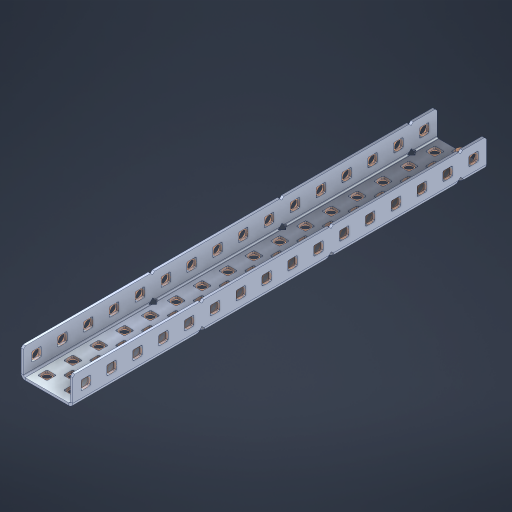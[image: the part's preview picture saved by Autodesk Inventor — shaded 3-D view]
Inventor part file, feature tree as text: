
AUTODESK INVENTOR PART (.ipt)
format: ipt  version: 2023 (Build 270158000, 158)  size: 1,214,976 bytes
history: native  units: in
note: dims shown in document units (in); Inventor stores cm internally (conversion verified against a paired STEP export)
features: other x87, extrude x78, sheet_metal_op x11, sketch x10, pattern_linear x2, mirror x1, chamfer x1
ambient origin geometry x8: Origin, YZ Plane, XZ Plane, XY Plane, X Axis, Y Axis, Z Axis, Center Point
bodies: Solid1 (feature_tree), Body (feature_tree)
feature tree (190):
  sheet_metal_op  "Flanges"
  other  "Flange Pattern Plane"
  other  "Flange Pattern Sketch"
  sheet_metal_op  "Flange Pattern"
  sheet_metal_op  "Body Pattern"
  pattern_linear  "Center Pattern"  Spacing1=0.0469in  [1 undecoded]
  other  "Arc Length"
  mirror  "Notch Mirror"
  pattern_linear  "Notch Pattern"  Spacing1=0.182in  [1 undecoded]
  chamfer  "End Chamfer"
  extrude  "Half Cut"  Depth=0.02in
  sketch  "Sketch1"  dims[d0=1.0in]
  other  "Plate1"
  sketch  "Sketch2"  dims[d1=8.0in]
  other  "Plate2"
  sheet_metal_op  "Bend1"
  sheet_metal_op  "Corner1"
  sketch  "Sketch3"  dims[d2=0.0469in]
  sketch  "Sketch7"  dims[d3=0.0469in]
  other  "Srf1"
  other  "Srf2"
  sketch  "Sketch8"  dims[d4=0.0234in]
  sketch  "Sketch9"  dims[d5=0.0938in]
  other  "Srf91"
  sheet_metal_op  "Body Pattern Sketch"
  other  "Srf92"
  sketch  "Sketch13"  dims[d6=0.0469in]
  sketch  "Sketch14"  dims[d7=0.5in d8=90.0deg d9=0.0312in]
  sketch  "Sketch15"  dims[d10=0.1875in]
  sketch  "Sketch16"  dims[d11=0.0469in d12=0.0469in d16=0.182in d17=0.02in d18=0.0469in d19=0.0in d20=0.25in d21=0.25in d38=6.2992in d40=0.5in d41=0.7874in d43=1.0in d46=0.172in d47=1.0in d48=0.0in d49=0.182in d50=0.02in d51=0.25in d52=0.25in d53=0.0469in d54=0.0in d55=0.172in d56=1.0in d57=0.0in d58=0.25in d60=6.2992in d62=0.5in d63=0.7874in d65=0.5in d85=0.1227in d86=0.1659in d88=0.04in d89=0.0469in d90=0.0in d91=0.04in d92=0.0491in d95=2.5in d96=0.04in d97=0.25in d98=45.0deg d99=0.25in d100=0.5in d101=0.0in d102=2.497in d106=0.182in d107=0.02in d108=0.5in d109=0.5in d110=0.0469in d111=0.0in d112=0.172in d113=0.5in d114=0.0in d117=0.5in d118=0.5in d119=0.5in]
  other  "Srf786"
  other  "Srf823"
  other  "Srf824"
  other  "Srf825"
  other  "Srf826"
  other  "Srf827"
  other  "Srf828"
  other  "Srf829"
  other  "Srf856"
  other  "Srf857"
  other  "Srf858"
  other  "Srf859"
  other  "Srf860"
  other  "Srf861"
  other  "Srf862"
  other  "Srf889"
  other  "Srf890"
  other  "Srf891"
  other  "Srf892"
  other  "Srf893"
  other  "Srf894"
  other  "Srf895"
  other  "Srf896"
  other  "Srf922"
  other  "Srf923"
  other  "Srf924"
  other  "Srf925"
  other  "Srf926"
  other  "Srf959"
  other  "Srf960"
  other  "Srf961"
  other  "Srf962"
  other  "Srf963"
  other  "Srf996"
  other  "Srf997"
  other  "Srf998"
  other  "Srf999"
  other  "Srf1000"
  other  "Srf1143"
  other  "Srf1144"
  other  "Srf1145"
  other  "Srf1146"
  other  "Srf1147"
  other  "Srf1148"
  other  "Srf1149"
  other  "Srf1150"
  other  "Srf1151"
  other  "Srf1152"
  other  "Srf1153"
  other  "Srf1154"
  other  "Srf1155"
  other  "Srf1156"
  other  "Srf1157"
  other  "Srf1158"
  other  "Srf1159"
  other  "Srf1160"
  other  "Srf1199"
  other  "Srf1200"
  other  "Srf1201"
  other  "Srf1202"
  other  "Srf1203"
  other  "Srf1204"
  other  "Srf1205"
  other  "Srf1206"
  other  "Srf1207"
  other  "Srf1208"
  other  "Srf1209"
  other  "Srf1210"
  other  "Srf1211"
  other  "Srf1212"
  other  "Srf1213"
  other  "Srf1214"
  other  "Srf1215"
  other  "Srf1216"
  other  "Srf1255"
  other  "Srf1256"
  sheet_metal_op  "Flange Stamp"
  sheet_metal_op  "Flange Circle"
  sheet_metal_op  "Body Stamp"
  sheet_metal_op  "Body Circle"
  other  "Center Stamp"
  other  "Center Circle"
  sheet_metal_op  "Notch"
  extrude  "ExtrusionSrf2"  Depth=0.0469in
  extrude  "ExtrusionSrf92"  TaperAngle=0.0deg  [1 undecoded]
  extrude  "ExtrusionSrf823"  Depth=0.5in
  extrude  "ExtrusionSrf824"  Depth=0.5in
  extrude  "ExtrusionSrf825"  Depth=0.5in
  extrude  "ExtrusionSrf826"  Depth=0.5in
  extrude  "ExtrusionSrf827"  Depth=1.0in TaperAngle=0.0deg
  extrude  "ExtrusionSrf828"  Depth=0.5in
  extrude  "ExtrusionSrf829"  Depth=0.02in
  extrude  "ExtrusionSrf856"  Depth=0.5in
  extrude  "ExtrusionSrf857"  Depth=0.5in
  extrude  "ExtrusionSrf858"  Depth=0.0469in
  extrude  "ExtrusionSrf859"  TaperAngle=0.0deg  [1 undecoded]
  extrude  "ExtrusionSrf860"  Depth=0.5in
  extrude  "ExtrusionSrf861"  Depth=1.0in TaperAngle=0.0deg
  extrude  "ExtrusionSrf862"  Depth=0.5in
  extrude  "ExtrusionSrf889"  Depth=0.5in
  extrude  "ExtrusionSrf890"  Depth=0.5in
  extrude  "ExtrusionSrf891"  Depth=0.5in
  extrude  "ExtrusionSrf892"  Depth=0.5in
  extrude  "ExtrusionSrf893"  Depth=0.5in
  extrude  "ExtrusionSrf894"  Depth=0.0469in
  extrude  "ExtrusionSrf895"  TaperAngle=0.0deg  [1 undecoded]
  extrude  "ExtrusionSrf896"  Depth=0.5in
  extrude  "ExtrusionSrf922"  Depth=0.5in
  extrude  "ExtrusionSrf923"  Depth=2.5in
  extrude  "ExtrusionSrf924"  Depth=0.5in TaperAngle=45.0deg
  extrude  "ExtrusionSrf925"  Depth=0.5in
  extrude  "ExtrusionSrf926"  Depth=0.5in TaperAngle=0.0deg
  extrude  "ExtrusionSrf959"  Depth=0.5in
  extrude  "ExtrusionSrf960"  Depth=0.5in
  extrude  "ExtrusionSrf961"  Depth=0.02in
  extrude  "ExtrusionSrf962"  Depth=0.5in
  extrude  "ExtrusionSrf963"  Depth=0.5in
  extrude  "ExtrusionSrf996"  Depth=0.0469in
  extrude  "ExtrusionSrf997"  TaperAngle=0.0deg  [1 undecoded]
  extrude  "ExtrusionSrf998"  Depth=0.5in
  extrude  "ExtrusionSrf999"  Depth=0.5in TaperAngle=0.0deg
  extrude  "ExtrusionSrf1000"  Depth=0.5in
  extrude  "ExtrusionSrf1143"  Depth=0.5in
  extrude  "ExtrusionSrf1144"  Depth=0.5in
  extrude  "ExtrusionSrf1145"  [1 undecoded]
  extrude  "ExtrusionSrf1146"  [1 undecoded]
  extrude  "ExtrusionSrf1147"  [1 undecoded]
  extrude  "ExtrusionSrf1148"  [1 undecoded]
  extrude  "ExtrusionSrf1149"  [1 undecoded]
  extrude  "ExtrusionSrf1150"  [1 undecoded]
  extrude  "ExtrusionSrf1151"  [1 undecoded]
  extrude  "ExtrusionSrf1152"  [1 undecoded]
  extrude  "ExtrusionSrf1153"  [1 undecoded]
  extrude  "ExtrusionSrf1154"  [1 undecoded]
  extrude  "ExtrusionSrf1155"  [1 undecoded]
  extrude  "ExtrusionSrf1156"  [1 undecoded]
  extrude  "ExtrusionSrf1157"  [1 undecoded]
  extrude  "ExtrusionSrf1158"  [1 undecoded]
  extrude  "ExtrusionSrf1159"  [1 undecoded]
  extrude  "ExtrusionSrf1160"  [1 undecoded]
  extrude  "ExtrusionSrf1199"  [1 undecoded]
  extrude  "ExtrusionSrf1200"  [1 undecoded]
  extrude  "ExtrusionSrf1201"  [1 undecoded]
  extrude  "ExtrusionSrf1202"  [1 undecoded]
  extrude  "ExtrusionSrf1203"  [1 undecoded]
  extrude  "ExtrusionSrf1204"  [1 undecoded]
  extrude  "ExtrusionSrf1205"  [1 undecoded]
  extrude  "ExtrusionSrf1206"  [1 undecoded]
  extrude  "ExtrusionSrf1207"  [1 undecoded]
  extrude  "ExtrusionSrf1208"  [1 undecoded]
  extrude  "ExtrusionSrf1209"  [1 undecoded]
  extrude  "ExtrusionSrf1210"  [1 undecoded]
  extrude  "ExtrusionSrf1211"  [1 undecoded]
  extrude  "ExtrusionSrf1212"  [1 undecoded]
  extrude  "ExtrusionSrf1213"  [1 undecoded]
  extrude  "ExtrusionSrf1214"  [1 undecoded]
  extrude  "ExtrusionSrf1215"  [1 undecoded]
  extrude  "ExtrusionSrf1216"  [1 undecoded]
  extrude  "ExtrusionSrf1255"  [1 undecoded]
  extrude  "ExtrusionSrf1256"  [1 undecoded]
note: 42 required parameter values undecoded (feature->parameter linkage not recoverable at this tier; creation-order binding heuristic only, values carry confidence <= 0.55)
